# Revit family: 32_Berkvens_Verdi WD70_stomp_v1.0
name_source: partatom
category: Doors
units: mm (PartAtom-declared; Revit-internal decimal feet)

## family parameters
Always vertical = Yes
Cut with Voids When Loaded = No
Host = Wall
OmniClass Number = 23.30.10.00
OmniClass Title = Doors
Room Calculation Point = Yes
Shared = No

## types (7) — shared parameters
60_45 Model kozijn = RZ enkeldeurs
60_63 Vloerplafondhoogte = 2610 mm  [stored 8.56299 ft]
60_81 Uitvoering kozijn = Kozijn plafondhoog WD70
60_84 Type kozijn = Verdi stalen montagekozijn
70_88 Uitvoering deur = standaard
70_90 Type deur = Berklon, lakdeur
80_30 Krukgathoogte = 1050 mm
80_60 Kantuitvoering = stomp
80_75 Deurhoogte = 2492 mm  [stored 8.17585 ft]
Analytic Construction = <None>
Assembly Code = 2E(32.31)
Compartmentation = No
FireExit = No
Function = Interior
IsExternal = No
M1 = Berkvens_kristalwit
M2 = Berkvens_kristalwit
Manufacturer = Berkvens
Model = Verdi RZ
SelfClosing = No
SmokeStop = No
URL = www.berkvens.nl
Versie = 1.0
Wall Closure = By host
zero-valued in all types: Height, Width

## per-type parameters (varying)
| type | 80_90 Deurbreedte actieve deur |
| 780 x VL-PL hoogte | 776 mm  [stored 2.54593 ft] |
| 730 x VL-PL hoogte | 726 mm  [stored 2.38189 ft] |
| 830 x VL-PL hoogte | 826 mm  [stored 2.70997 ft] |
| 880 x VL-PL hoogte | 876 mm  [stored 2.87402 ft] |
| 930 x VL-PL hoogte | 926 mm  [stored 3.03806 ft] |
| 980 x VL-PL hoogte (980 = meerprijs) | 976 mm  [stored 3.2021 ft] |
| 1030 x VL-PL hoogte (1030 = meerprijs) | 1026 mm  [stored 3.36614 ft] |

note: [stored X ft] marks values corroborated as IEEE doubles in the binary element streams (Revit-internal decimal feet)

## geometry (parser evidence)
native form markers: Sweep x22
no freeform markers — native parametric forms only
